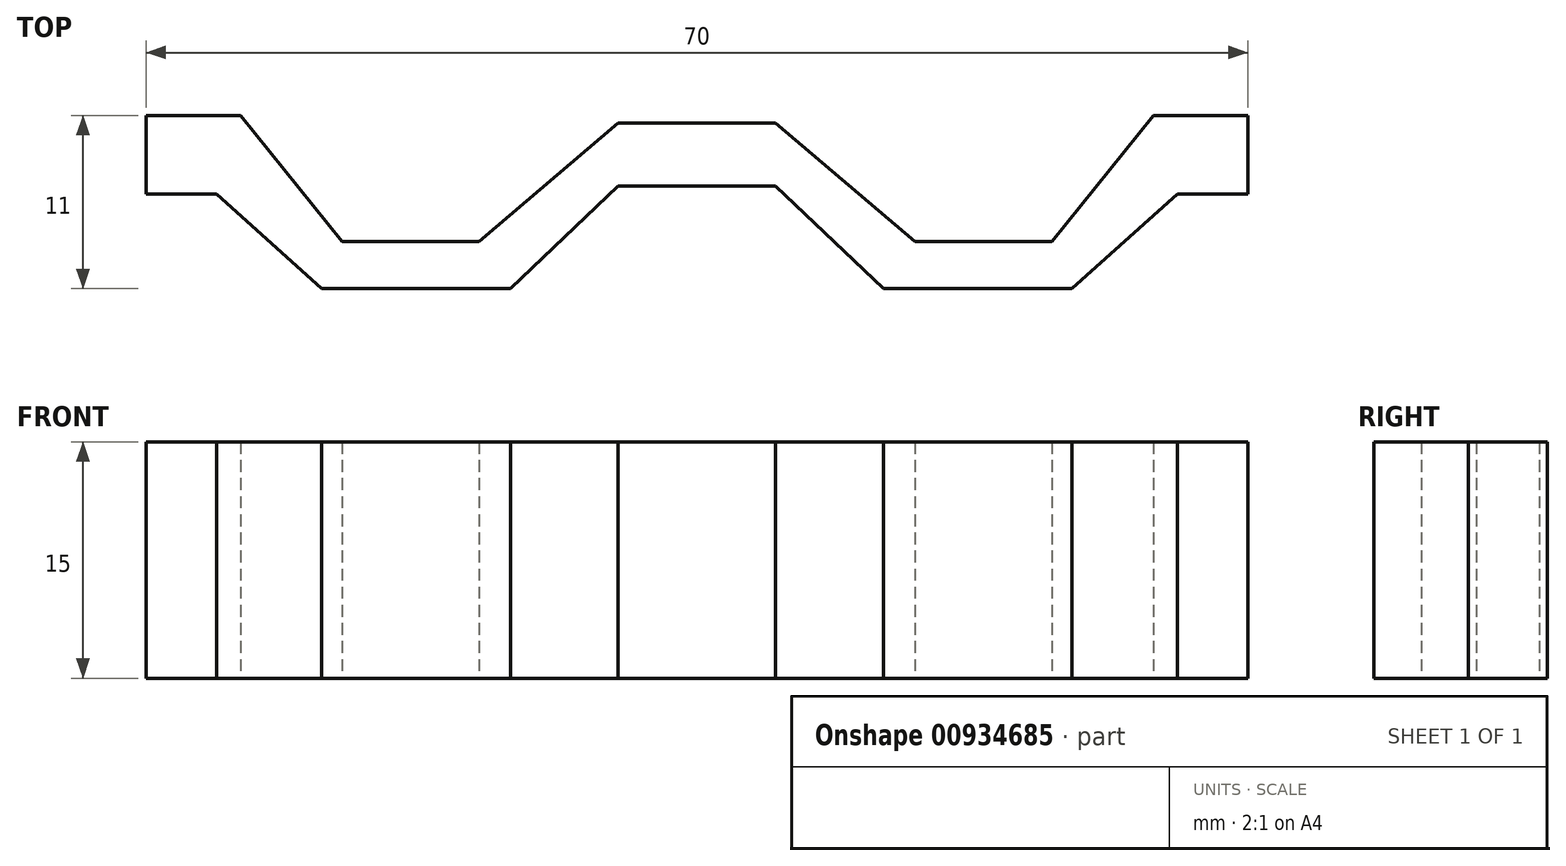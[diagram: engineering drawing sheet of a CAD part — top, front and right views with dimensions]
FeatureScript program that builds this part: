
annotation { "Feature Type Name" : "Feature", "Feature Type Description" : "" }
export const myFeature = defineFeature(function(context is Context, id is Id, definition is map)
    precondition{}
    {
        {
            var Q0;
            Q0=qCreatedBy(makeId("Top.planeOp"),FACE);
            var sketch = newSketch(context, id + "F0", { "sketchPlane" : qUnion([Q0])});
            skLineSegment(sketch, "E0", {"start": v(0, 7.5) * mm, "end": v(-5, 7.5) * mm});
            skLineSegment(sketch, "E1", {"start": v(-5, 7.5) * mm, "end": v(-13.83, 0) * mm});
            skLineSegment(sketch, "E2", {"start": v(-13.83, 0) * mm, "end": v(-22.55, 0) * mm});
            skLineSegment(sketch, "E3", {"start": v(-22.55, 0) * mm, "end": v(-29, 8) * mm});
            skLineSegment(sketch, "E4", {"start": v(-29, 8) * mm, "end": v(-35, 8) * mm});
            skLineSegment(sketch, "E5", {"start": v(-35, 8) * mm, "end": v(-35, 3) * mm});
            skLineSegment(sketch, "E6", {"start": v(-35, 3) * mm, "end": v(-30.5, 3) * mm});
            skLineSegment(sketch, "E7", {"start": v(-30.5, 3) * mm, "end": v(-23.83, -3) * mm});
            skLineSegment(sketch, "E8", {"start": v(-23.83, -3) * mm, "end": v(-11.83, -3) * mm});
            skLineSegment(sketch, "E9", {"start": v(-11.83, -3) * mm, "end": v(-5, 3.5) * mm});
            skLineSegment(sketch, "E10", {"start": v(-5, 3.5) * mm, "end": v(0, 3.5) * mm});
            skLineSegment(sketch, "E11.MirrorCS", {"start": v(0, 7.5) * mm, "end": v(5, 7.5) * mm});
            skLineSegment(sketch, "E12.MirrorCS", {"start": v(5, 7.5) * mm, "end": v(13.83, 0) * mm});
            skLineSegment(sketch, "E13.MirrorCS", {"start": v(13.83, 0) * mm, "end": v(22.55, 0) * mm});
            skLineSegment(sketch, "E14.MirrorCS", {"start": v(22.55, 0) * mm, "end": v(29, 8) * mm});
            skLineSegment(sketch, "E15.MirrorCS", {"start": v(29, 8) * mm, "end": v(35, 8) * mm});
            skLineSegment(sketch, "E16.MirrorCS", {"start": v(35, 8) * mm, "end": v(35, 3) * mm});
            skLineSegment(sketch, "E17.MirrorCS", {"start": v(35, 3) * mm, "end": v(30.5, 3) * mm});
            skLineSegment(sketch, "E18.MirrorCS", {"start": v(30.5, 3) * mm, "end": v(23.83, -3) * mm});
            skLineSegment(sketch, "E19.MirrorCS", {"start": v(23.83, -3) * mm, "end": v(11.83, -3) * mm});
            skLineSegment(sketch, "E20.MirrorCS", {"start": v(11.83, -3) * mm, "end": v(5, 3.5) * mm});
            skLineSegment(sketch, "E21.MirrorCS", {"start": v(5, 3.5) * mm, "end": v(0, 3.5) * mm});
            skSolve(sketch);
        }
        {
            var Q0;
            Q0 = qSketchRegion(id + "F0", true);
            extrude(context, id + "F1", {"entities" : qUnion([Q0]), "depth" : 15 * mm, "offsetDistance" : 25 * mm});
        }
    });
